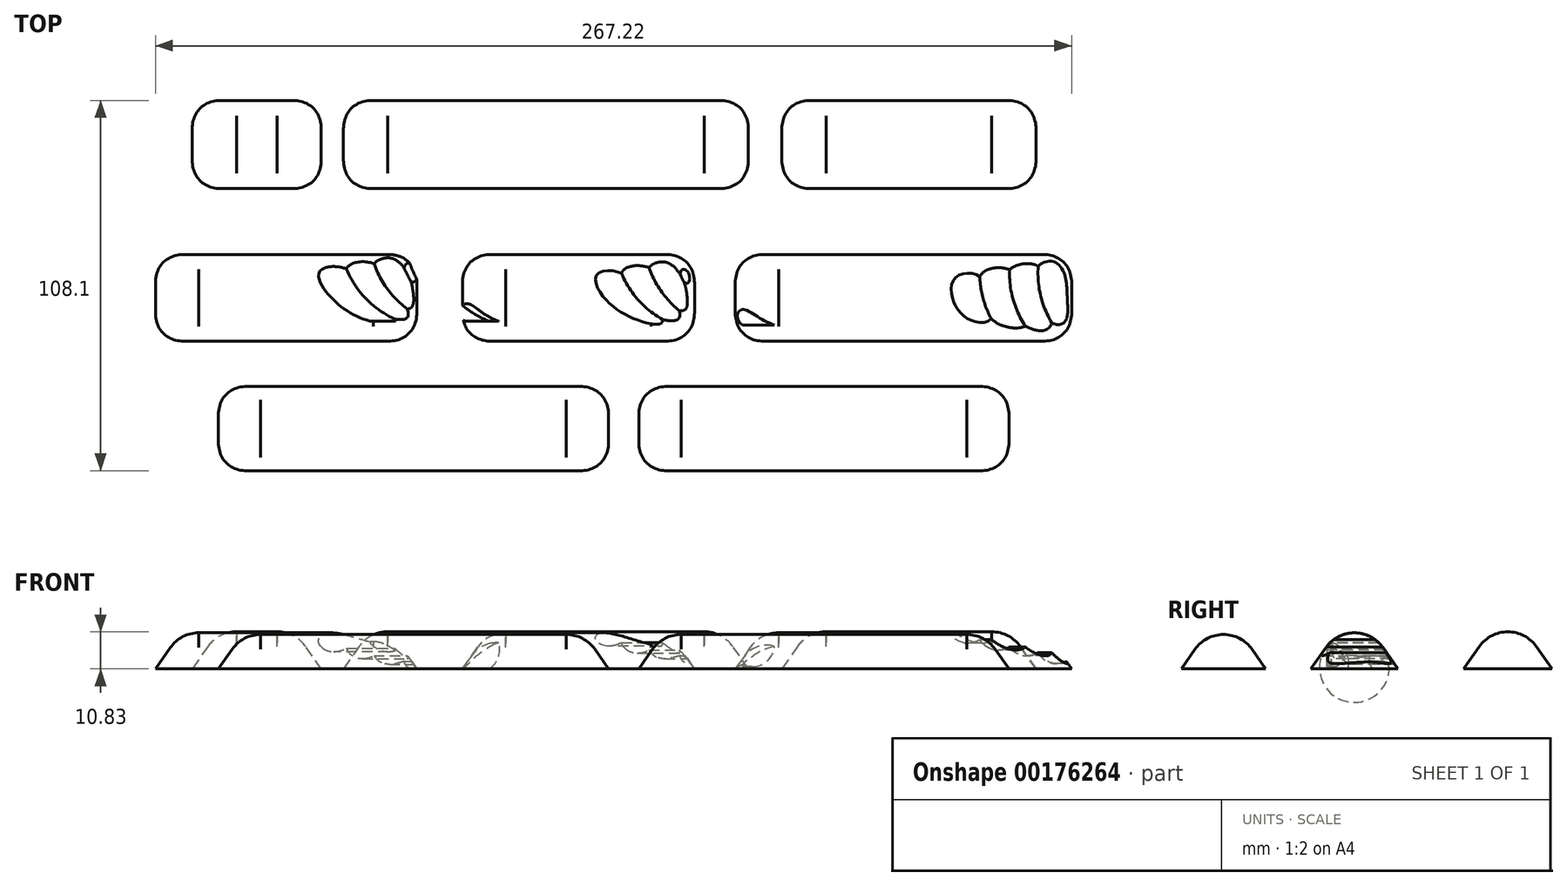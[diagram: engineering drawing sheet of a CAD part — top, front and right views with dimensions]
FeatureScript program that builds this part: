
annotation { "Feature Type Name" : "Feature", "Feature Type Description" : "" }
export const myFeature = defineFeature(function(context is Context, id is Id, definition is map)
    precondition{}
    {
        {
            var Q0;
            Q0=qCreatedBy(makeId("Top.planeOp"),FACE);
            var sketch = newSketch(context, id + "F0", { "sketchPlane" : qUnion([Q0])});
            skLineSegment(sketch, "E0.bottom", {"start": v(126.23, -33.5) * mm, "end": v(28.13, -33.5) * mm});
            skLineSegment(sketch, "E0.top", {"start": v(126.23, -8.2) * mm, "end": v(28.13, -8.2) * mm});
            skLineSegment(sketch, "E0.left", {"start": v(126.23, -33.5) * mm, "end": v(126.23, -8.2) * mm});
            skLineSegment(sketch, "E0.right", {"start": v(28.13, -33.5) * mm, "end": v(28.13, -8.2) * mm});
            skLineSegment(sketch, "E1.bottom", {"start": v(16.23, -33.5) * mm, "end": v(-51.43, -33.5) * mm});
            skLineSegment(sketch, "E1.top", {"start": v(16.23, -8.2) * mm, "end": v(-51.43, -8.2) * mm});
            skLineSegment(sketch, "E1.left", {"start": v(16.23, -33.5) * mm, "end": v(16.23, -8.2) * mm});
            skLineSegment(sketch, "E1.right", {"start": v(-51.43, -33.5) * mm, "end": v(-51.43, -8.2) * mm});
            skLineSegment(sketch, "E2.bottom", {"start": v(-64.75, -33.5) * mm, "end": v(-141, -33.5) * mm});
            skLineSegment(sketch, "E2.top", {"start": v(-64.75, -8.2) * mm, "end": v(-141, -8.2) * mm});
            skLineSegment(sketch, "E2.left", {"start": v(-64.75, -33.5) * mm, "end": v(-64.75, -8.2) * mm});
            skLineSegment(sketch, "E2.right", {"start": v(-141, -33.5) * mm, "end": v(-141, -8.2) * mm});
            skLineSegment(sketch, "E3.bottom", {"start": v(115.82, 11.04) * mm, "end": v(41.72, 11.04) * mm});
            skLineSegment(sketch, "E3.top", {"start": v(115.82, 36.78) * mm, "end": v(41.72, 36.78) * mm});
            skLineSegment(sketch, "E3.left", {"start": v(115.82, 11.04) * mm, "end": v(115.82, 36.78) * mm});
            skLineSegment(sketch, "E3.right", {"start": v(41.72, 11.04) * mm, "end": v(41.72, 36.78) * mm});
            skLineSegment(sketch, "E4.bottom", {"start": v(31.94, 11.04) * mm, "end": v(-86.14, 11.04) * mm});
            skLineSegment(sketch, "E4.top", {"start": v(31.94, 36.78) * mm, "end": v(-86.14, 36.78) * mm});
            skLineSegment(sketch, "E4.left", {"start": v(31.94, 11.04) * mm, "end": v(31.94, 36.78) * mm});
            skLineSegment(sketch, "E4.right", {"start": v(-86.14, 11.04) * mm, "end": v(-86.14, 36.78) * mm});
            skLineSegment(sketch, "E5.bottom", {"start": v(-92.63, 11.04) * mm, "end": v(-130.25, 11.04) * mm});
            skLineSegment(sketch, "E5.top", {"start": v(-92.63, 36.78) * mm, "end": v(-130.25, 36.78) * mm});
            skLineSegment(sketch, "E5.left", {"start": v(-92.63, 11.04) * mm, "end": v(-92.63, 36.78) * mm});
            skLineSegment(sketch, "E5.right", {"start": v(-130.25, 11.04) * mm, "end": v(-130.25, 36.78) * mm});
            skLineSegment(sketch, "E6.bottom", {"start": v(107.94, -46.72) * mm, "end": v(0, -46.72) * mm});
            skLineSegment(sketch, "E6.top", {"start": v(107.94, -71.32) * mm, "end": v(0, -71.32) * mm});
            skLineSegment(sketch, "E6.left", {"start": v(107.94, -46.72) * mm, "end": v(107.94, -71.32) * mm});
            skLineSegment(sketch, "E6.right", {"start": v(0, -46.72) * mm, "end": v(0, -71.32) * mm});
            skLineSegment(sketch, "E7.bottom", {"start": v(-8.84, -71.32) * mm, "end": v(-122.62, -71.32) * mm});
            skLineSegment(sketch, "E7.top", {"start": v(-8.84, -46.72) * mm, "end": v(-122.62, -46.72) * mm});
            skLineSegment(sketch, "E7.left", {"start": v(-8.84, -71.32) * mm, "end": v(-8.84, -46.72) * mm});
            skLineSegment(sketch, "E7.right", {"start": v(-122.62, -71.32) * mm, "end": v(-122.62, -46.72) * mm});
            skSolve(sketch);
        }
        {
            var Q0;
            Q0 = qSketchRegion(id + "F0", true);
            extrude(context, id + "F1", {"entities" : qUnion([Q0]), "depth" : 20.32 * mm, "hasDraft" : true, "draftAngle" : 35 * degree, "draftPullDirection" : true});
        }
        {
            var Q0;
            Q0=makeQuery(id+"F1.*.draft.opDraft","TWEAK_EDGE",EDGE,{"derivedFrom":[makeQuery(id+"F1.opExtrude","SWEPT_FACE",FACE,{"disambiguationData":[OSD([sQuery(id+"F0.wireOp",EDGE,"E6.bottom")])]}),makeQuery(id+"F1.opExtrude","SWEPT_FACE",FACE,{"disambiguationData":[OSD([sQuery(id+"F0.wireOp",EDGE,"E6.top")])]})]});
            var Q1;
            Q1=makeQuery(id+"F1.opExtrude","SWEPT_EDGE",EDGE,{"disambiguationData":[OSD([sQuery(id+"F0.wireOp",EDGE,"E6.bottom"),sQuery(id+"F0.wireOp",EDGE,"E6.left")])]});
            var Q2;
            Q2=makeQuery(id+"F1.opExtrude","SWEPT_EDGE",EDGE,{"disambiguationData":[OSD([sQuery(id+"F0.wireOp",EDGE,"E6.top"),sQuery(id+"F0.wireOp",EDGE,"E6.left")])]});
            var Q3;
            Q3=makeQuery(id+"F1.opExtrude","SWEPT_EDGE",EDGE,{"disambiguationData":[OSD([sQuery(id+"F0.wireOp",EDGE,"E6.bottom"),sQuery(id+"F0.wireOp",EDGE,"E6.right")])]});
            var Q4;
            Q4=makeQuery(id+"F1.opExtrude","SWEPT_EDGE",EDGE,{"disambiguationData":[OSD([sQuery(id+"F0.wireOp",EDGE,"E6.top"),sQuery(id+"F0.wireOp",EDGE,"E6.right")])]});
            var Q5;
            Q5=makeQuery(id+"F1.opExtrude","SWEPT_EDGE",EDGE,{"disambiguationData":[OSD([sQuery(id+"F0.wireOp",EDGE,"E7.top"),sQuery(id+"F0.wireOp",EDGE,"E7.left")])]});
            var Q6;
            Q6=makeQuery(id+"F1.opExtrude","SWEPT_EDGE",EDGE,{"disambiguationData":[OSD([sQuery(id+"F0.wireOp",EDGE,"E7.bottom"),sQuery(id+"F0.wireOp",EDGE,"E7.left")])]});
            var Q7;
            Q7=makeQuery(id+"F1.*.draft.opDraft","TWEAK_EDGE",EDGE,{"derivedFrom":[makeQuery(id+"F1.opExtrude","SWEPT_FACE",FACE,{"disambiguationData":[OSD([sQuery(id+"F0.wireOp",EDGE,"E7.bottom")])]}),makeQuery(id+"F1.opExtrude","SWEPT_FACE",FACE,{"disambiguationData":[OSD([sQuery(id+"F0.wireOp",EDGE,"E7.top")])]})]});
            var Q8;
            Q8=makeQuery(id+"F1.opExtrude","SWEPT_EDGE",EDGE,{"disambiguationData":[OSD([sQuery(id+"F0.wireOp",EDGE,"E7.top"),sQuery(id+"F0.wireOp",EDGE,"E7.right")])]});
            var Q9;
            Q9=makeQuery(id+"F1.opExtrude","SWEPT_EDGE",EDGE,{"disambiguationData":[OSD([sQuery(id+"F0.wireOp",EDGE,"E7.bottom"),sQuery(id+"F0.wireOp",EDGE,"E7.right")])]});
            var Q10;
            Q10=makeQuery(id+"F1.opExtrude","SWEPT_EDGE",EDGE,{"disambiguationData":[OSD([sQuery(id+"F0.wireOp",EDGE,"E0.top"),sQuery(id+"F0.wireOp",EDGE,"E0.left")])]});
            var Q11;
            Q11=makeQuery(id+"F1.opExtrude","SWEPT_EDGE",EDGE,{"disambiguationData":[OSD([sQuery(id+"F0.wireOp",EDGE,"E0.bottom"),sQuery(id+"F0.wireOp",EDGE,"E0.left")])]});
            var Q12;
            Q12=makeQuery(id+"F1.*.draft.opDraft","TWEAK_EDGE",EDGE,{"derivedFrom":[makeQuery(id+"F1.opExtrude","SWEPT_FACE",FACE,{"disambiguationData":[OSD([sQuery(id+"F0.wireOp",EDGE,"E0.bottom")])]}),makeQuery(id+"F1.opExtrude","SWEPT_FACE",FACE,{"disambiguationData":[OSD([sQuery(id+"F0.wireOp",EDGE,"E0.top")])]})]});
            var Q13;
            Q13=makeQuery(id+"F1.opExtrude","SWEPT_EDGE",EDGE,{"disambiguationData":[OSD([sQuery(id+"F0.wireOp",EDGE,"E0.bottom"),sQuery(id+"F0.wireOp",EDGE,"E0.right")])]});
            var Q14;
            Q14=makeQuery(id+"F1.opExtrude","SWEPT_EDGE",EDGE,{"disambiguationData":[OSD([sQuery(id+"F0.wireOp",EDGE,"E0.top"),sQuery(id+"F0.wireOp",EDGE,"E0.right")])]});
            var Q15;
            Q15=makeQuery(id+"F1.opExtrude","SWEPT_EDGE",EDGE,{"disambiguationData":[OSD([sQuery(id+"F0.wireOp",EDGE,"E1.bottom"),sQuery(id+"F0.wireOp",EDGE,"E1.left")])]});
            var Q16;
            Q16=makeQuery(id+"F1.opExtrude","SWEPT_EDGE",EDGE,{"disambiguationData":[OSD([sQuery(id+"F0.wireOp",EDGE,"E1.top"),sQuery(id+"F0.wireOp",EDGE,"E1.left")])]});
            var Q17;
            Q17=makeQuery(id+"F1.*.draft.opDraft","TWEAK_EDGE",EDGE,{"derivedFrom":[makeQuery(id+"F1.opExtrude","SWEPT_FACE",FACE,{"disambiguationData":[OSD([sQuery(id+"F0.wireOp",EDGE,"E1.bottom")])]}),makeQuery(id+"F1.opExtrude","SWEPT_FACE",FACE,{"disambiguationData":[OSD([sQuery(id+"F0.wireOp",EDGE,"E1.top")])]})]});
            var Q18;
            Q18=makeQuery(id+"F1.opExtrude","SWEPT_EDGE",EDGE,{"disambiguationData":[OSD([sQuery(id+"F0.wireOp",EDGE,"E1.top"),sQuery(id+"F0.wireOp",EDGE,"E1.right")])]});
            var Q19;
            Q19=makeQuery(id+"F1.opExtrude","SWEPT_EDGE",EDGE,{"disambiguationData":[OSD([sQuery(id+"F0.wireOp",EDGE,"E1.bottom"),sQuery(id+"F0.wireOp",EDGE,"E1.right")])]});
            var Q20;
            Q20=makeQuery(id+"F1.opExtrude","SWEPT_EDGE",EDGE,{"disambiguationData":[OSD([sQuery(id+"F0.wireOp",EDGE,"E2.bottom"),sQuery(id+"F0.wireOp",EDGE,"E2.left")])]});
            var Q21;
            Q21=makeQuery(id+"F1.opExtrude","SWEPT_EDGE",EDGE,{"disambiguationData":[OSD([sQuery(id+"F0.wireOp",EDGE,"E2.top"),sQuery(id+"F0.wireOp",EDGE,"E2.left")])]});
            var Q22;
            Q22=makeQuery(id+"F1.*.draft.opDraft","TWEAK_EDGE",EDGE,{"derivedFrom":[makeQuery(id+"F1.opExtrude","SWEPT_FACE",FACE,{"disambiguationData":[OSD([sQuery(id+"F0.wireOp",EDGE,"E2.bottom")])]}),makeQuery(id+"F1.opExtrude","SWEPT_FACE",FACE,{"disambiguationData":[OSD([sQuery(id+"F0.wireOp",EDGE,"E2.top")])]})]});
            var Q23;
            Q23=makeQuery(id+"F1.opExtrude","SWEPT_EDGE",EDGE,{"disambiguationData":[OSD([sQuery(id+"F0.wireOp",EDGE,"E2.top"),sQuery(id+"F0.wireOp",EDGE,"E2.right")])]});
            var Q24;
            Q24=makeQuery(id+"F1.opExtrude","SWEPT_EDGE",EDGE,{"disambiguationData":[OSD([sQuery(id+"F0.wireOp",EDGE,"E2.bottom"),sQuery(id+"F0.wireOp",EDGE,"E2.right")])]});
            var Q25;
            Q25=makeQuery(id+"F1.opExtrude","SWEPT_EDGE",EDGE,{"disambiguationData":[OSD([sQuery(id+"F0.wireOp",EDGE,"E3.top"),sQuery(id+"F0.wireOp",EDGE,"E3.left")])]});
            var Q26;
            Q26=makeQuery(id+"F1.opExtrude","SWEPT_EDGE",EDGE,{"disambiguationData":[OSD([sQuery(id+"F0.wireOp",EDGE,"E3.bottom"),sQuery(id+"F0.wireOp",EDGE,"E3.left")])]});
            var Q27;
            Q27=makeQuery(id+"F1.*.draft.opDraft","TWEAK_EDGE",EDGE,{"derivedFrom":[makeQuery(id+"F1.opExtrude","SWEPT_FACE",FACE,{"disambiguationData":[OSD([sQuery(id+"F0.wireOp",EDGE,"E3.bottom")])]}),makeQuery(id+"F1.opExtrude","SWEPT_FACE",FACE,{"disambiguationData":[OSD([sQuery(id+"F0.wireOp",EDGE,"E3.top")])]})]});
            var Q28;
            Q28=makeQuery(id+"F1.opExtrude","SWEPT_EDGE",EDGE,{"disambiguationData":[OSD([sQuery(id+"F0.wireOp",EDGE,"E3.top"),sQuery(id+"F0.wireOp",EDGE,"E3.right")])]});
            var Q29;
            Q29=makeQuery(id+"F1.opExtrude","SWEPT_EDGE",EDGE,{"disambiguationData":[OSD([sQuery(id+"F0.wireOp",EDGE,"E3.bottom"),sQuery(id+"F0.wireOp",EDGE,"E3.right")])]});
            var Q30;
            Q30=makeQuery(id+"F1.opExtrude","SWEPT_EDGE",EDGE,{"disambiguationData":[OSD([sQuery(id+"F0.wireOp",EDGE,"E4.bottom"),sQuery(id+"F0.wireOp",EDGE,"E4.left")])]});
            var Q31;
            Q31=makeQuery(id+"F1.*.draft.opDraft","TWEAK_EDGE",EDGE,{"derivedFrom":[makeQuery(id+"F1.opExtrude","SWEPT_FACE",FACE,{"disambiguationData":[OSD([sQuery(id+"F0.wireOp",EDGE,"E4.bottom")])]}),makeQuery(id+"F1.opExtrude","SWEPT_FACE",FACE,{"disambiguationData":[OSD([sQuery(id+"F0.wireOp",EDGE,"E4.top")])]})]});
            var Q32;
            Q32=makeQuery(id+"F1.opExtrude","SWEPT_EDGE",EDGE,{"disambiguationData":[OSD([sQuery(id+"F0.wireOp",EDGE,"E4.top"),sQuery(id+"F0.wireOp",EDGE,"E4.left")])]});
            var Q33;
            Q33=makeQuery(id+"F1.opExtrude","SWEPT_EDGE",EDGE,{"disambiguationData":[OSD([sQuery(id+"F0.wireOp",EDGE,"E4.top"),sQuery(id+"F0.wireOp",EDGE,"E4.right")])]});
            var Q34;
            Q34=makeQuery(id+"F1.opExtrude","SWEPT_EDGE",EDGE,{"disambiguationData":[OSD([sQuery(id+"F0.wireOp",EDGE,"E4.bottom"),sQuery(id+"F0.wireOp",EDGE,"E4.right")])]});
            var Q35;
            Q35=makeQuery(id+"F1.opExtrude","SWEPT_EDGE",EDGE,{"disambiguationData":[OSD([sQuery(id+"F0.wireOp",EDGE,"E5.bottom"),sQuery(id+"F0.wireOp",EDGE,"E5.left")])]});
            var Q36;
            Q36=makeQuery(id+"F1.opExtrude","SWEPT_EDGE",EDGE,{"disambiguationData":[OSD([sQuery(id+"F0.wireOp",EDGE,"E5.top"),sQuery(id+"F0.wireOp",EDGE,"E5.left")])]});
            var Q37;
            Q37=makeQuery(id+"F1.*.draft.opDraft","TWEAK_EDGE",EDGE,{"derivedFrom":[makeQuery(id+"F1.opExtrude","SWEPT_FACE",FACE,{"disambiguationData":[OSD([sQuery(id+"F0.wireOp",EDGE,"E5.bottom")])]}),makeQuery(id+"F1.opExtrude","SWEPT_FACE",FACE,{"disambiguationData":[OSD([sQuery(id+"F0.wireOp",EDGE,"E5.top")])]})]});
            var Q38;
            Q38=makeQuery(id+"F1.opExtrude","SWEPT_EDGE",EDGE,{"disambiguationData":[OSD([sQuery(id+"F0.wireOp",EDGE,"E5.top"),sQuery(id+"F0.wireOp",EDGE,"E5.right")])]});
            var Q39;
            Q39=makeQuery(id+"F1.opExtrude","SWEPT_EDGE",EDGE,{"disambiguationData":[OSD([sQuery(id+"F0.wireOp",EDGE,"E5.bottom"),sQuery(id+"F0.wireOp",EDGE,"E5.right")])]});
            fillet(context, id + "F2", {"entities" : qUnion([Q0, Q1, Q2, Q3, Q4, Q5, Q6, Q7, Q8, Q9, Q10, Q11, Q12, Q13, Q14, Q15, Q16, Q17, Q18, Q19, Q20, Q21, Q22, Q23, Q24, Q25, Q26, Q27, Q28, Q29, Q30, Q31, Q32, Q33, Q34, Q35, Q36, Q37, Q38, Q39]), "radius" : 10.16 * mm, "tangentPropagation" : true, "allowEdgeOverflow" : false});
        }
        {
            var Q0;
            Q0=qCreatedBy(makeId("Front.planeOp"),FACE);
            var sketch = newSketch(context, id + "F3", { "sketchPlane" : qUnion([Q0])});
            skCircle(sketch, "E8", {"center": v(116.81, 10.16) * mm, "radius": 6.35 * mm});
            skCircle(sketch, "E9", {"center": v(108.53, 12) * mm, "radius": 6.5 * mm});
            skCircle(sketch, "E10", {"center": v(125.64, 8) * mm, "radius": 6.5 * mm});
            skCircle(sketch, "E11", {"center": v(99.63, 14) * mm, "radius": 6.5 * mm});
            skCircle(sketch, "E12", {"center": v(6.72, 9.3) * mm, "radius": 6.35 * mm});
            skCircle(sketch, "E13", {"center": v(-1.56, 11.14) * mm, "radius": 6.5 * mm});
            skCircle(sketch, "E14", {"center": v(15.55, 7.14) * mm, "radius": 6.5 * mm});
            skCircle(sketch, "E15", {"center": v(-10.46, 13.14) * mm, "radius": 6.5 * mm});
            skCircle(sketch, "E16", {"center": v(-73.58, 7.67) * mm, "radius": 6.35 * mm});
            skCircle(sketch, "E17", {"center": v(-81.86, 9.5) * mm, "radius": 6.5 * mm});
            skCircle(sketch, "E18", {"center": v(-64.75, 5.5) * mm, "radius": 6.5 * mm});
            skCircle(sketch, "E19", {"center": v(-90.76, 11.5) * mm, "radius": 6.5 * mm});
            skSolve(sketch);
        }
        {
            var Q0;
            Q0=qCreatedBy(makeId("Top.planeOp"),FACE);
            cPlane(context, id + "F4", {"entities" : qUnion([Q0]), "cplaneType" : CPlaneType.OFFSET, "offset" : 10.16 * mm, "width" : 152.4 * mm, "height" : 152.4 * mm});
        }
        {
            var Q0;
            Q0=qCreatedBy(id+"F4.planeOp",FACE);
            var sketch = newSketch(context, id + "F5", { "sketchPlane" : qUnion([Q0])});
            skArc(sketch, "E20", {"start": v(123.85, -0.15) * mm, "mid": v(121.81, -23.14) * mm, "end": v(137.93, -39.66) * mm});
            skSolve(sketch);
        }
        {
            var Q0;
            Q0 = qSketchRegion(id + "F3", true);
            var Q1;
            Q1=sQuery(id+"F5.wireOp",EDGE,"E20");
            sweep(context, id + "F6", {"profiles" : qUnion([Q0]), "path" : qUnion([Q1]), "keepProfileOrientation" : true});
        }
        {
            var Q0;
            Q0=makeQuery(id+"F6.opSweep","SWEPT_BODY",BODY,{"disambiguationData":[OSD([sQuery(id+"F3.wireOp",EDGE,"E8"),sQuery(id+"F5.wireOp",EDGE,"E20")])]});
            var Q1;
            Q1=makeQuery(id+"F6.opSweep","SWEPT_BODY",BODY,{"disambiguationData":[OSD([sQuery(id+"F3.wireOp",EDGE,"E12"),sQuery(id+"F3.wireOp",EDGE,"E13"),sQuery(id+"F3.wireOp",EDGE,"E14"),sQuery(id+"F3.wireOp",EDGE,"E15"),sQuery(id+"F5.wireOp",EDGE,"E20")])]});
            var Q2;
            Q2=makeQuery(id+"F6.opSweep","SWEPT_BODY",BODY,{"disambiguationData":[OSD([sQuery(id+"F3.wireOp",EDGE,"E16"),sQuery(id+"F3.wireOp",EDGE,"E17"),sQuery(id+"F3.wireOp",EDGE,"E18"),sQuery(id+"F3.wireOp",EDGE,"E19"),sQuery(id+"F5.wireOp",EDGE,"E20")])]});
            var Q3;
            Q3=makeQuery(id+"F1.opExtrude","SWEPT_BODY",BODY,{"disambiguationData":[OSD([sQuery(id+"F0.wireOp",EDGE,"E0.bottom"),sQuery(id+"F0.wireOp",EDGE,"E0.top"),sQuery(id+"F0.wireOp",EDGE,"E0.left"),sQuery(id+"F0.wireOp",EDGE,"E0.right")])]});
            var Q4;
            Q4=makeQuery(id+"F1.opExtrude","SWEPT_BODY",BODY,{"disambiguationData":[OSD([sQuery(id+"F0.wireOp",EDGE,"E1.bottom"),sQuery(id+"F0.wireOp",EDGE,"E1.top"),sQuery(id+"F0.wireOp",EDGE,"E1.left"),sQuery(id+"F0.wireOp",EDGE,"E1.right")])]});
            var Q5;
            Q5=makeQuery(id+"F1.opExtrude","SWEPT_BODY",BODY,{"disambiguationData":[OSD([sQuery(id+"F0.wireOp",EDGE,"E2.bottom"),sQuery(id+"F0.wireOp",EDGE,"E2.top"),sQuery(id+"F0.wireOp",EDGE,"E2.left"),sQuery(id+"F0.wireOp",EDGE,"E2.right")])]});
            booleanBodies(context, id + "F7", {"operationType" : BooleanOperationType.SUBTRACTION, "tools" : qUnion([Q0, Q1, Q2]), "targets" : qUnion([Q3, Q4, Q5])});
        }
    });
